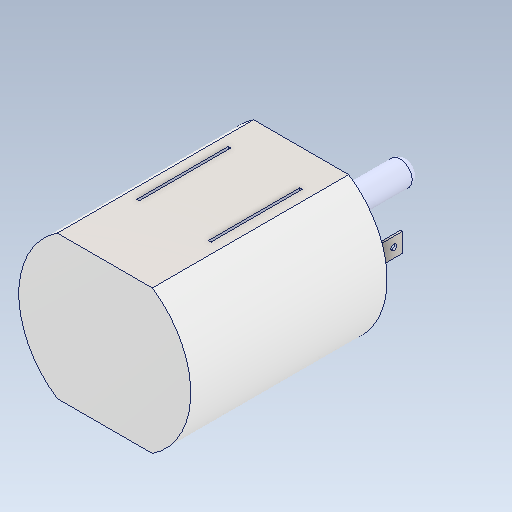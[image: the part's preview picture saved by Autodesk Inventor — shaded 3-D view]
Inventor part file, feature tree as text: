
AUTODESK INVENTOR PART (.ipt)
format: ipt  version: 2020 (Build 240168000, 168)  size: 120,832 bytes
history: mixed  units: in
note: dims shown in document units (in); Inventor stores cm internally (conversion verified against a paired STEP export)
features: fillet x1, imported_body x1
ambient origin geometry x8: Origin, YZ Plane, XZ Plane, XY Plane, X Axis, Y Axis, Z Axis, Center Point
bodies: Solid1 (imported_parasolid)
feature tree (2):
  fillet  "Redondeo1"  [1 undecoded]
  imported_body  NMx_Import_Brep_tag  [imported B-rep: ~30 faces, bbox_mm=[8.573189, 10.0, 16.5]]
note: 1 required parameter value undecoded (feature->parameter linkage not recoverable at this tier; creation-order binding heuristic only, values carry confidence <= 0.55)
